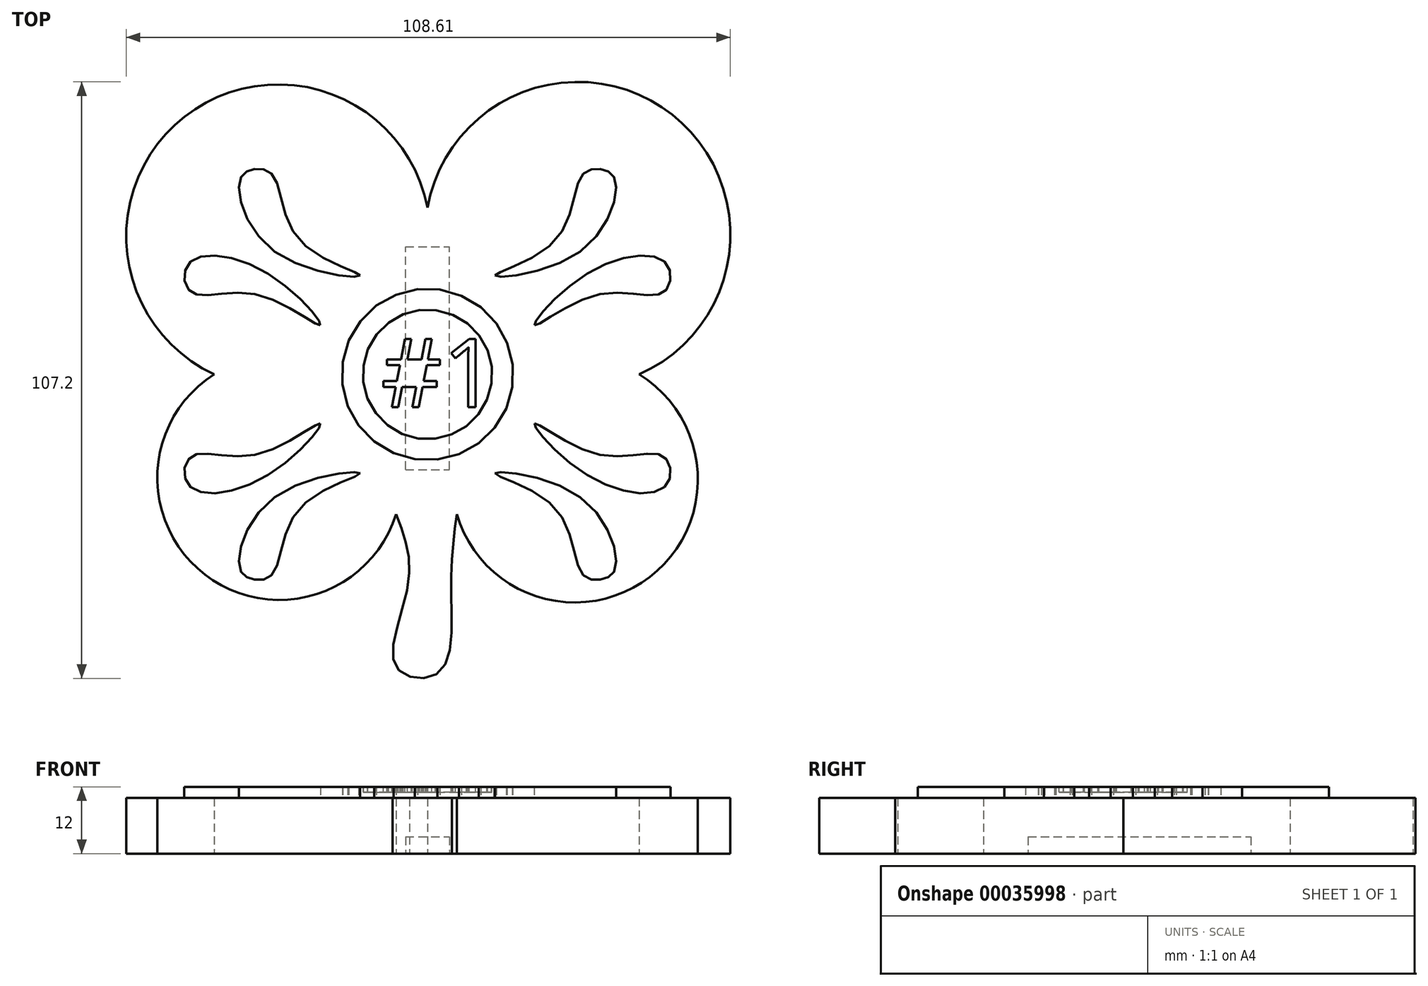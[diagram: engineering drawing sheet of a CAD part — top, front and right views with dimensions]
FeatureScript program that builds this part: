
annotation { "Feature Type Name" : "Feature", "Feature Type Description" : "" }
export const myFeature = defineFeature(function(context is Context, id is Id, definition is map)
    precondition{}
    {
        {
            var Q0;
            Q0=qCreatedBy(makeId("Top.planeOp"),FACE);
            var sketch = newSketch(context, id + "F0", { "sketchPlane" : qUnion([Q0])});
            skArc(sketch, "E0", {"start": v(38.05, 0) * mm, "mid": v(44, 46.68) * mm, "end": v(0, 29.97) * mm});
            skArc(sketch, "E1", {"start": v(0, 29.97) * mm, "mid": v(-43.66, 46.32) * mm, "end": v(-38.34, 0) * mm});
            skArc(sketch, "E2", {"start": v(5.25, -25.12) * mm, "mid": v(39.93, -36.43) * mm, "end": v(38.05, 0) * mm});
            skArc(sketch, "E3", {"start": v(-38.34, 0) * mm, "mid": v(-40, -35.99) * mm, "end": v(-5.65, -25.12) * mm});
            skFitSpline(sketch, "E4", {"points": [v(-5.65, -25.12) * mm, v(-3.43, -37.43) * mm, v(-5.65, -52.57) * mm, v(2.02, -53.58) * mm, v(4.24, -38.84) * mm, v(5.25, -25.12) * mm], "startDerivative": vector(22.02, -56.56) * mm, "endDerivative": vector(7.74, 60.43) * mm});
            skSolve(sketch);
        }
        {
            var Q0;
            Q0 = qSketchRegion(id + "F0", true);
            extrude(context, id + "F1", {"entities" : qUnion([Q0]), "depth" : 10 * mm});
        }
        {
            var Q0;
            Q0=makeQuery(id+"F1.opExtrude","CAP_FACE",FACE,{"disambiguationData":[OSD([sQuery(id+"F0.wireOp",EDGE,"E0"),sQuery(id+"F0.wireOp",EDGE,"E1"),sQuery(id+"F0.wireOp",EDGE,"E2"),sQuery(id+"F0.wireOp",EDGE,"E3"),sQuery(id+"F0.wireOp",EDGE,"E4")])],"isStart":false});
            var sketch = newSketch(context, id + "F2", { "sketchPlane" : qUnion([Q0])});
            skFitSpline(sketch, "E5", {"points": [v(-12.12, 17.78) * mm, v(-22.84, 23.93) * mm, v(-27.8, 35.85) * mm, v(-31.38, 36.84) * mm, v(-33.76, 34.86) * mm, v(-27.01, 21.75) * mm, v(-12.12, 17.78) * mm]});
            skFitSpline(sketch, "E6", {"points": [v(-19.27, 8.84) * mm, v(-28.8, 18.17) * mm, v(-42.9, 19.96) * mm, v(-42.5, 14.8) * mm, v(-30.78, 14.4) * mm, v(-19.27, 8.84) * mm]});
            skFitSpline(sketch, "E7.MirrorC", {"points": [v(19.27, 8.84) * mm, v(28.8, 18.17) * mm, v(42.9, 19.96) * mm, v(42.5, 14.8) * mm, v(30.78, 14.4) * mm, v(19.27, 8.84) * mm]});
            skFitSpline(sketch, "E8.MirrorC", {"points": [v(12.12, 17.78) * mm, v(22.84, 23.93) * mm, v(27.8, 35.85) * mm, v(31.38, 36.84) * mm, v(33.76, 34.86) * mm, v(27.01, 21.75) * mm, v(12.12, 17.78) * mm]});
            skFitSpline(sketch, "E9.MirrorC", {"points": [v(19.27, -8.84) * mm, v(28.8, -18.17) * mm, v(42.9, -19.96) * mm, v(42.5, -14.8) * mm, v(30.78, -14.4) * mm, v(19.27, -8.84) * mm]});
            skFitSpline(sketch, "E10.MirrorC", {"points": [v(12.12, -17.78) * mm, v(22.84, -23.93) * mm, v(27.8, -35.85) * mm, v(31.38, -36.84) * mm, v(33.76, -34.86) * mm, v(27.01, -21.75) * mm, v(12.12, -17.78) * mm]});
            skFitSpline(sketch, "E11.MirrorC", {"points": [v(-19.27, -8.84) * mm, v(-28.8, -18.17) * mm, v(-42.9, -19.96) * mm, v(-42.5, -14.8) * mm, v(-30.78, -14.4) * mm, v(-19.27, -8.84) * mm]});
            skFitSpline(sketch, "E12.MirrorC", {"points": [v(-12.12, -17.78) * mm, v(-22.84, -23.93) * mm, v(-27.8, -35.85) * mm, v(-31.38, -36.84) * mm, v(-33.76, -34.86) * mm, v(-27.01, -21.75) * mm, v(-12.12, -17.78) * mm]});
            skSolve(sketch);
        }
        {
            var Q0;
            Q0 = qSketchRegion(id + "F2", true);
            extrude(context, id + "F3", {"entities" : qUnion([Q0]), "operationType" : NewBodyOperationType.ADD, "depth" : 2 * mm});
        }
        {
            var Q0;
            Q0=makeQuery(id+"F1.opExtrude","CAP_FACE",FACE,{"disambiguationData":[OSD([sQuery(id+"F0.wireOp",EDGE,"E0"),sQuery(id+"F0.wireOp",EDGE,"E1"),sQuery(id+"F0.wireOp",EDGE,"E2"),sQuery(id+"F0.wireOp",EDGE,"E3"),sQuery(id+"F0.wireOp",EDGE,"E4")])],"isStart":true});
            var sketch = newSketch(context, id + "F4", { "sketchPlane" : qUnion([Q0])});
            skLineSegment(sketch, "E13", {"start": v(0, 17.12) * mm, "end": v(-3.95, 17.12) * mm});
            skLineSegment(sketch, "E14", {"start": v(-3.95, 17.12) * mm, "end": v(-3.95, -22.96) * mm});
            skLineSegment(sketch, "E15", {"start": v(-3.95, -22.96) * mm, "end": v(0, -22.96) * mm});
            skLineSegment(sketch, "E16.MirrorCS", {"start": v(0, 17.12) * mm, "end": v(3.95, 17.12) * mm});
            skLineSegment(sketch, "E17.MirrorCS", {"start": v(3.95, 17.12) * mm, "end": v(3.95, -22.96) * mm});
            skLineSegment(sketch, "E18.MirrorCS", {"start": v(3.95, -22.96) * mm, "end": v(0, -22.96) * mm});
            skSolve(sketch);
        }
        {
            var Q0;
            Q0 = qSketchRegion(id + "F4", true);
            extrude(context, id + "F5", {"entities" : qUnion([Q0]), "operationType" : NewBodyOperationType.REMOVE, "oppositeDirection" : true, "depth" : 3 * mm});
        }
        {
            var Q0;
            Q0=makeQuery(id+"F1.opExtrude","CAP_FACE",FACE,{"disambiguationData":[OSD([sQuery(id+"F0.wireOp",EDGE,"E0"),sQuery(id+"F0.wireOp",EDGE,"E1"),sQuery(id+"F0.wireOp",EDGE,"E2"),sQuery(id+"F0.wireOp",EDGE,"E3"),sQuery(id+"F0.wireOp",EDGE,"E4")])],"isStart":false});
            var sketch = newSketch(context, id + "F6", { "sketchPlane" : qUnion([Q0])});
            skCircle(sketch, "E19.cCircle", {"center": v(0, 0) * mm, "radius": 15.28 * mm, "construction": true});
            skLineSegment(sketch, "E19.0", {"start": v(14.14, -6.12) * mm, "end": v(12.08, -9.57) * mm});
            skLineSegment(sketch, "E19.1", {"start": v(12.08, -9.57) * mm, "end": v(9.19, -12.37) * mm});
            skLineSegment(sketch, "E19.2", {"start": v(9.19, -12.37) * mm, "end": v(5.67, -14.33) * mm});
            skLineSegment(sketch, "E19.3", {"start": v(5.67, -14.33) * mm, "end": v(1.77, -15.3) * mm});
            skLineSegment(sketch, "E19.4", {"start": v(1.77, -15.3) * mm, "end": v(-2.25, -15.24) * mm});
            skLineSegment(sketch, "E19.5", {"start": v(-2.25, -15.24) * mm, "end": v(-6.12, -14.14) * mm});
            skLineSegment(sketch, "E19.6", {"start": v(-6.12, -14.14) * mm, "end": v(-9.57, -12.08) * mm});
            skLineSegment(sketch, "E19.7", {"start": v(-9.57, -12.08) * mm, "end": v(-12.37, -9.19) * mm});
            skLineSegment(sketch, "E19.8", {"start": v(-12.37, -9.19) * mm, "end": v(-14.33, -5.67) * mm});
            skLineSegment(sketch, "E19.9", {"start": v(-14.33, -5.67) * mm, "end": v(-15.3, -1.77) * mm});
            skLineSegment(sketch, "E19.10", {"start": v(-15.3, -1.77) * mm, "end": v(-15.24, 2.25) * mm});
            skLineSegment(sketch, "E19.11", {"start": v(-15.24, 2.25) * mm, "end": v(-14.14, 6.12) * mm});
            skLineSegment(sketch, "E19.12", {"start": v(-14.14, 6.12) * mm, "end": v(-12.08, 9.57) * mm});
            skLineSegment(sketch, "E19.13", {"start": v(-12.08, 9.57) * mm, "end": v(-9.19, 12.37) * mm});
            skLineSegment(sketch, "E19.14", {"start": v(-9.19, 12.37) * mm, "end": v(-5.67, 14.33) * mm});
            skLineSegment(sketch, "E19.15", {"start": v(-5.67, 14.33) * mm, "end": v(-1.77, 15.3) * mm});
            skLineSegment(sketch, "E19.16", {"start": v(-1.77, 15.3) * mm, "end": v(2.25, 15.24) * mm});
            skLineSegment(sketch, "E19.17", {"start": v(2.25, 15.24) * mm, "end": v(6.12, 14.14) * mm});
            skLineSegment(sketch, "E19.18", {"start": v(6.12, 14.14) * mm, "end": v(9.57, 12.08) * mm});
            skLineSegment(sketch, "E19.19", {"start": v(9.57, 12.08) * mm, "end": v(12.37, 9.19) * mm});
            skLineSegment(sketch, "E19.20", {"start": v(12.37, 9.19) * mm, "end": v(14.33, 5.67) * mm});
            skLineSegment(sketch, "E19.21", {"start": v(14.33, 5.67) * mm, "end": v(15.3, 1.77) * mm});
            skLineSegment(sketch, "E19.22", {"start": v(15.3, 1.77) * mm, "end": v(15.24, -2.25) * mm});
            skLineSegment(sketch, "E19.23", {"start": v(15.24, -2.25) * mm, "end": v(14.14, -6.12) * mm});
            skPoint(sketch, "E19.0.midPoint", {"position": v(13.1, -7.85) * mm});
            skSolve(sketch);
        }
        {
            var Q0;
            Q0 = qSketchRegion(id + "F6", true);
            extrude(context, id + "F7", {"entities" : qUnion([Q0]), "operationType" : NewBodyOperationType.ADD, "depth" : 2 * mm});
        }
        {
            var Q0;
            Q0=makeQuery(id+"F7.opExtrude","CAP_FACE",FACE,{"disambiguationData":[OSD([sQuery(id+"F6.wireOp",EDGE,"E19.0"),sQuery(id+"F6.wireOp",EDGE,"E19.1"),sQuery(id+"F6.wireOp",EDGE,"E19.2"),sQuery(id+"F6.wireOp",EDGE,"E19.3"),sQuery(id+"F6.wireOp",EDGE,"E19.4"),sQuery(id+"F6.wireOp",EDGE,"E19.5"),sQuery(id+"F6.wireOp",EDGE,"E19.6"),sQuery(id+"F6.wireOp",EDGE,"E19.7"),sQuery(id+"F6.wireOp",EDGE,"E19.8"),sQuery(id+"F6.wireOp",EDGE,"E19.9"),sQuery(id+"F6.wireOp",EDGE,"E19.10"),sQuery(id+"F6.wireOp",EDGE,"E19.11"),sQuery(id+"F6.wireOp",EDGE,"E19.12"),sQuery(id+"F6.wireOp",EDGE,"E19.13"),sQuery(id+"F6.wireOp",EDGE,"E19.14"),sQuery(id+"F6.wireOp",EDGE,"E19.15"),sQuery(id+"F6.wireOp",EDGE,"E19.16"),sQuery(id+"F6.wireOp",EDGE,"E19.17"),sQuery(id+"F6.wireOp",EDGE,"E19.18"),sQuery(id+"F6.wireOp",EDGE,"E19.19"),sQuery(id+"F6.wireOp",EDGE,"E19.20"),sQuery(id+"F6.wireOp",EDGE,"E19.21"),sQuery(id+"F6.wireOp",EDGE,"E19.22"),sQuery(id+"F6.wireOp",EDGE,"E19.23")])],"isStart":false});
            var sketch = newSketch(context, id + "F8", { "sketchPlane" : qUnion([Q0])});
            skCircle(sketch, "E20.cCircle", {"center": v(0, 0) * mm, "radius": 11.53 * mm, "construction": true});
            skLineSegment(sketch, "E20.0", {"start": v(10.7, -4.55) * mm, "end": v(9.16, -7.17) * mm});
            skLineSegment(sketch, "E20.1", {"start": v(9.16, -7.17) * mm, "end": v(7, -9.3) * mm});
            skLineSegment(sketch, "E20.2", {"start": v(7, -9.3) * mm, "end": v(4.35, -10.79) * mm});
            skLineSegment(sketch, "E20.3", {"start": v(4.35, -10.79) * mm, "end": v(1.4, -11.54) * mm});
            skLineSegment(sketch, "E20.4", {"start": v(1.4, -11.54) * mm, "end": v(-1.63, -11.52) * mm});
            skLineSegment(sketch, "E20.5", {"start": v(-1.63, -11.52) * mm, "end": v(-4.55, -10.7) * mm});
            skLineSegment(sketch, "E20.6", {"start": v(-4.55, -10.7) * mm, "end": v(-7.17, -9.16) * mm});
            skLineSegment(sketch, "E20.7", {"start": v(-7.17, -9.16) * mm, "end": v(-9.3, -7) * mm});
            skLineSegment(sketch, "E20.8", {"start": v(-9.3, -7) * mm, "end": v(-10.79, -4.35) * mm});
            skLineSegment(sketch, "E20.9", {"start": v(-10.79, -4.35) * mm, "end": v(-11.54, -1.4) * mm});
            skLineSegment(sketch, "E20.10", {"start": v(-11.54, -1.4) * mm, "end": v(-11.52, 1.63) * mm});
            skLineSegment(sketch, "E20.11", {"start": v(-11.52, 1.63) * mm, "end": v(-10.7, 4.55) * mm});
            skLineSegment(sketch, "E20.12", {"start": v(-10.7, 4.55) * mm, "end": v(-9.16, 7.17) * mm});
            skLineSegment(sketch, "E20.13", {"start": v(-9.16, 7.17) * mm, "end": v(-7, 9.3) * mm});
            skLineSegment(sketch, "E20.14", {"start": v(-7, 9.3) * mm, "end": v(-4.35, 10.79) * mm});
            skLineSegment(sketch, "E20.15", {"start": v(-4.35, 10.79) * mm, "end": v(-1.4, 11.54) * mm});
            skLineSegment(sketch, "E20.16", {"start": v(-1.4, 11.54) * mm, "end": v(1.63, 11.52) * mm});
            skLineSegment(sketch, "E20.17", {"start": v(1.63, 11.52) * mm, "end": v(4.55, 10.7) * mm});
            skLineSegment(sketch, "E20.18", {"start": v(4.55, 10.7) * mm, "end": v(7.17, 9.16) * mm});
            skLineSegment(sketch, "E20.19", {"start": v(7.17, 9.16) * mm, "end": v(9.3, 7) * mm});
            skLineSegment(sketch, "E20.20", {"start": v(9.3, 7) * mm, "end": v(10.79, 4.35) * mm});
            skLineSegment(sketch, "E20.21", {"start": v(10.79, 4.35) * mm, "end": v(11.54, 1.4) * mm});
            skLineSegment(sketch, "E20.22", {"start": v(11.54, 1.4) * mm, "end": v(11.52, -1.63) * mm});
            skLineSegment(sketch, "E20.23", {"start": v(11.52, -1.63) * mm, "end": v(10.7, -4.55) * mm});
            skPoint(sketch, "E20.0.midPoint", {"position": v(9.93, -5.86) * mm});
            skText(sketch, "E21", { "text": "#1", "fontName": "OpenSans-Regular.ttf"});
            const initialGuessF8  = {"E21": [-0.00834, -0.00586, 1, 0, 0.01231]};
            skSetInitialGuess(sketch, initialGuessF8);
            skSolve(sketch);
        }
        {
            var Q0;
            Q0 = qSketchRegion(id + "F8", true);
            extrude(context, id + "F9", {"entities" : qUnion([Q0]), "operationType" : NewBodyOperationType.REMOVE, "oppositeDirection" : true, "depth" : 1 * mm});
        }
    });
